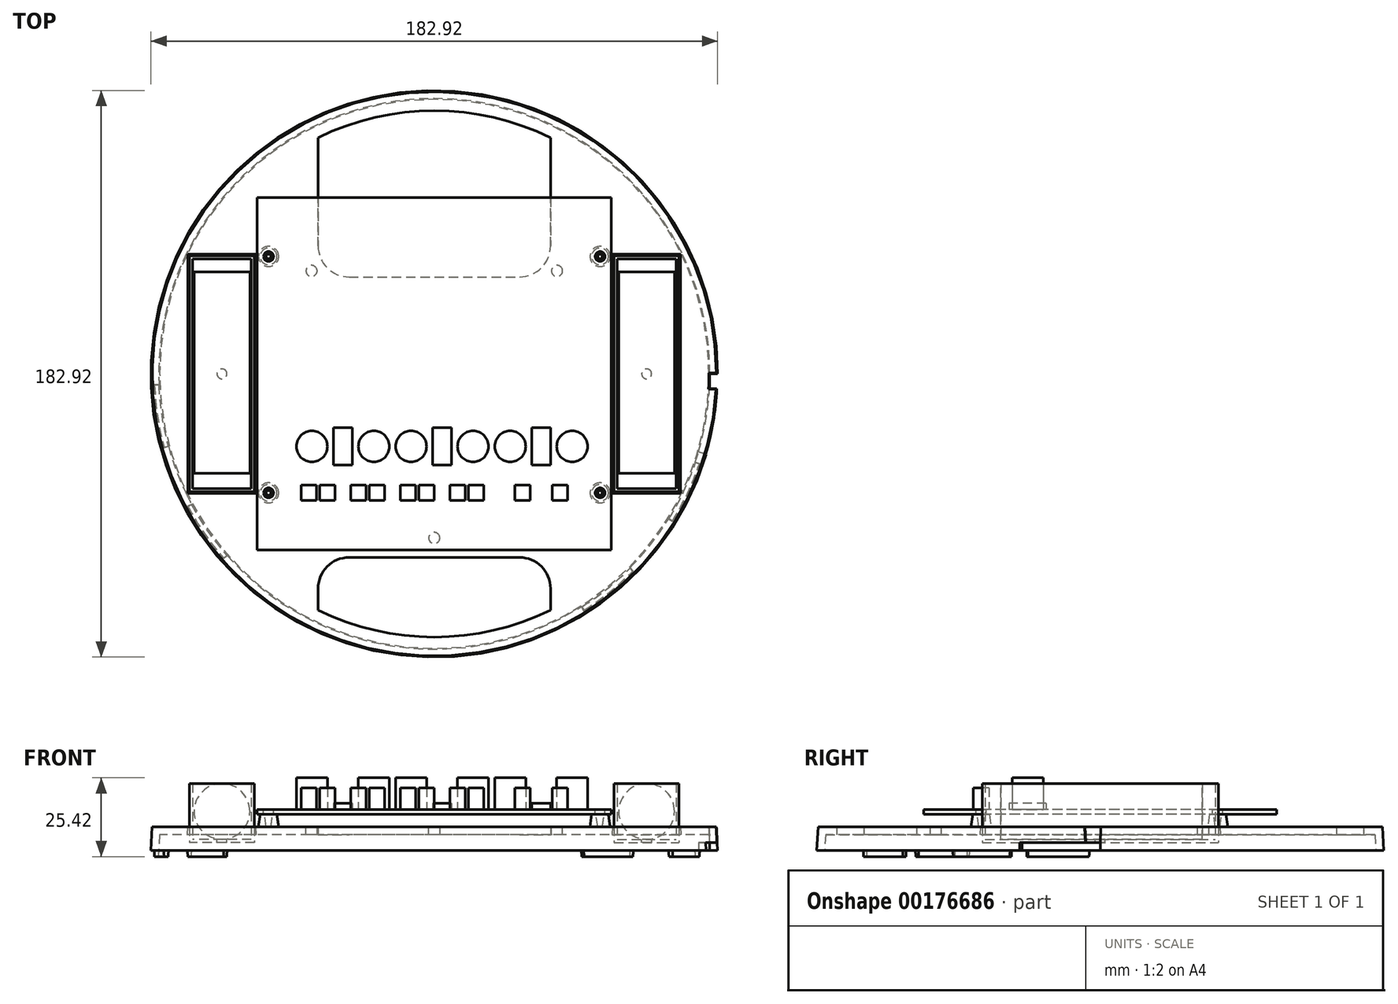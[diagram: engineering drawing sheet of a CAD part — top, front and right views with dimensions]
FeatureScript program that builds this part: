
annotation { "Feature Type Name" : "Feature", "Feature Type Description" : "" }
export const myFeature = defineFeature(function(context is Context, id is Id, definition is map)
    precondition{}
    {
        {
            assignVariable(context, id + "F0", {"name" : "h_env", "anyValue" : 230});
        }
        {
            var Q0;
            Q0=qCreatedBy(makeId("Top.planeOp"),FACE);
            var sketch = newSketch(context, id + "F1", { "sketchPlane" : qUnion([Q0])});
            skCircle(sketch, "E0", {"center": v(0, 0) * mm, "radius": 94 * mm});
            skSolve(sketch);
        }
        {
            var Q0;
            Q0=qCreatedBy(makeId("Top.planeOp"),FACE);
            cPlane(context, id + "F2", {"entities" : qUnion([Q0]), "cplaneType" : CPlaneType.OFFSET, "offset" : (getVariable(context, 'h_env')) * mm, "width" : 152.4 * mm, "height" : 152.4 * mm});
        }
        {
            var Q0;
            Q0=makeQuery(id+"F1.imprint","IMPRINT",FACE,{"disambiguationData":[TD([[makeQuery(id+"F1.imprint","IMPRINT",EDGE,{"derivedFrom":sQuery(id+"F1.wireOp",EDGE,"E0")}),1.0]])]});
            var Q1;
            Q1=sQuery(id+"F1.wireOp",EDGE,"E0");
            var Q2;
            Q2=qCreatedBy(id+"F2.planeOp",FACE);
            extrude(context, id + "F3", {"entities" : qUnion([Q0]), "bodyType" : ToolBodyType.SURFACE, "surfaceEntities" : qUnion([Q1]), "endBound" : BoundingType.UP_TO_SURFACE, "endBoundEntityFace" : qUnion([Q2]), "depth" : 25.4 * mm});
        }
        {
            var Q0;
            Q0=qCreatedBy(makeId("Right.planeOp"),FACE);
            var sketch = newSketch(context, id + "F4", { "sketchPlane" : qUnion([Q0])});
            skLineSegment(sketch, "E1", {"start": v(0, 0) * mm, "end": v(0, 230) * mm, "construction": true});
            skSolve(sketch);
        }
        {
            assignVariable(context, id + "F5", {"name" : "t", "anyValue" : 2.54});
        }
        {
            assignVariable(context, id + "F6", {"name" : "h_primary", "anyValue" : 19.05});
        }
        {
            assignVariable(context, id + "F7", {"name" : "draft", "anyValue" : 3});
        }
        {
            var Q0;
            Q0=qCreatedBy(id+"F2.planeOp",FACE);
            cPlane(context, id + "F8", {"entities" : qUnion([Q0]), "cplaneType" : CPlaneType.OFFSET, "offset" : (getVariable(context, 'h_primary')) * mm, "oppositeDirection" : true, "width" : 152.4 * mm, "height" : 152.4 * mm});
        }
        {
            var Q0;
            Q0=qCreatedBy(id+"F8.planeOp",FACE);
            var sketch = newSketch(context, id + "F9", { "sketchPlane" : qUnion([Q0])});
            skCircle(sketch, "E2", {"center": v(0, 0) * mm, "radius": 91.46 * mm});
            skSolve(sketch);
        }
        {
            var Q0;
            Q0=makeQuery(id+"F9.imprint","IMPRINT",FACE,{"disambiguationData":[TD([[makeQuery(id+"F9.imprint","IMPRINT",EDGE,{"derivedFrom":sQuery(id+"F9.wireOp",EDGE,"E2")}),1.0]])]});
            extrude(context, id + "F10", {"entities" : qUnion([Q0]), "depth" : (3 * getVariable(context, 't')) * mm, "hasDraft" : true, "draftAngle" : (getVariable(context, 'draft')) * degree, "draftPullDirection" : true});
        }
        {
            var Q0;
            Q0=makeQuery(id+"F10.opExtrude","CAP_FACE",FACE,{"disambiguationData":[OSD([sQuery(id+"F9.wireOp",EDGE,"E2")])],"isStart":true});
            shell(context, id + "F11", {"entities" : qUnion([Q0]), "thickness" : (getVariable(context, 't')) * mm});
        }
        {
            var Q0;
            Q0=makeQuery(id+"F10.opExtrude","CAP_FACE",FACE,{"disambiguationData":[OSD([sQuery(id+"F9.wireOp",EDGE,"E2")])],"isStart":true});
            var sketch = newSketch(context, id + "F12", { "sketchPlane" : qUnion([Q0])});
            skLineSegment(sketch, "E3", {"start": v(0, 0) * mm, "end": v(88.34, 23.67) * mm, "construction": true});
            skLineSegment(sketch, "E4", {"start": v(0, 0) * mm, "end": v(91.46, 0) * mm, "construction": true});
            skLineSegment(sketch, "E5", {"start": v(0, 0) * mm, "end": v(87.7, 25.98) * mm, "construction": true});
            skCircle(sketch, "E6.0", {"center": v(0, 0) * mm, "radius": 88.65 * mm});
            skArc(sketch, "E7", {"start": v(88.65, 0) * mm, "mid": v(87.73, 12.72) * mm, "end": v(85, 25.18) * mm});
            skLineSegment(sketch, "E8", {"start": v(87.7, 25.98) * mm, "end": v(85, 25.18) * mm});
            skLineSegment(sketch, "E9", {"start": v(91.46, 0) * mm, "end": v(88.65, 0) * mm});
            skSolve(sketch);
        }
        {
            var Q0;
            {var subQ0=sQuery(id+"F12.wireOp",EDGE,"E8");var subQ1=sQuery(id+"F9.wireOp",EDGE,"E2");var subQ2=makeQuery(id+"F10.opExtrude","CAP_EDGE",EDGE,{"disambiguationData":[OSD([subQ1])],"isStart":true});var subQ3=makeQuery(id+"F12.imprint","INTERSECT",VERTEX,{"derivedFrom":[subQ2,subQ0]});Q0=makeQuery(id+"F12.imprint","IMPRINT",FACE,{"disambiguationData":[TD([[makeQuery(id+"F12.imprint","IMPRINT",EDGE,{"disambiguationData":[TD([[subQ3,-1.0]])],"derivedFrom":subQ2}),-1.0]])]});}
            var Q1;
            {var subQ0=sQuery(id+"F12.wireOp",EDGE,"E8");var subQ1=sQuery(id+"F12.wireOp",EDGE,"E6.0");var subQ2=makeQuery(id+"F12.imprint","INTERSECT",VERTEX,{"derivedFrom":[subQ1,subQ0]});Q1=makeQuery(id+"F12.imprint","IMPRINT",FACE,{"disambiguationData":[TD([[makeQuery(id+"F12.imprint","IMPRINT",EDGE,{"disambiguationData":[TD([[subQ2,-1.0]])],"derivedFrom":subQ1}),1.0]])]});}
            extrude(context, id + "F13", {"entities" : qUnion([Q0, Q1]), "operationType" : NewBodyOperationType.REMOVE, "oppositeDirection" : true, "depth" : (getVariable(context, 't')) * mm});
        }
        {
            var Q0;
            Q0=makeQuery(id+"F13.boolean.opBoolean","COPY",FACE,{"derivedFrom":makeQuery(id+"F13.opExtrude","CAP_FACE",FACE,{"disambiguationData":[OSD([sQuery(id+"F9.wireOp",EDGE,"E2"),sQuery(id+"F12.wireOp",EDGE,"E6.0"),sQuery(id+"F12.wireOp",EDGE,"E8"),sQuery(id+"F12.wireOp",EDGE,"E9")])],"isStart":false})});
            var sketch = newSketch(context, id + "F14", { "sketchPlane" : qUnion([Q0])});
            skArc(sketch, "E10.0", {"start": v(91.33, 0) * mm, "mid": v(90.38, 13.1) * mm, "end": v(87.57, 25.94) * mm});
            skCircle(sketch, "E11.0", {"center": v(0, 0) * mm, "radius": 88.65 * mm});
            skLineSegment(sketch, "E12.0", {"start": v(91.33, 0) * mm, "end": v(88.65, 0) * mm});
            skPoint(sketch, "E13.orphan", {"position": v(88.78, 0) * mm});
            skLineSegment(sketch, "E14", {"start": v(0, 0) * mm, "end": v(91.33, 0) * mm, "construction": true});
            skLineSegment(sketch, "E15", {"start": v(0, 0) * mm, "end": v(91.2, 4.78) * mm, "construction": true});
            skLineSegment(sketch, "E16", {"start": v(91.2, 4.78) * mm, "end": v(88.53, 4.64) * mm});
            skSolve(sketch);
        }
        {
            var Q0;
            {var subQ0=sQuery(id+"F14.wireOp",EDGE,"E12.0");var subQ1=sQuery(id+"F14.wireOp",EDGE,"E10.0");var subQ2=makeQuery(id+"F14.imprint","INTERSECT",VERTEX,{"derivedFrom":[subQ1,subQ0]});Q0=makeQuery(id+"F14.imprint","IMPRINT",FACE,{"disambiguationData":[TD([[makeQuery(id+"F14.imprint","IMPRINT",EDGE,{"disambiguationData":[TD([[subQ2,-1.0]])],"derivedFrom":subQ1}),1.0]])]});}
            var Q1;
            Q1=makeQuery(id+"F10.opExtrude","CAP_FACE",FACE,{"disambiguationData":[OSD([sQuery(id+"F9.wireOp",EDGE,"E2")])],"isStart":false});
            extrude(context, id + "F15", {"entities" : qUnion([Q0]), "operationType" : NewBodyOperationType.REMOVE, "endBound" : BoundingType.UP_TO_SURFACE, "oppositeDirection" : true, "endBoundEntityFace" : qUnion([Q1]), "depth" : 25 * mm, "hasDraft" : true, "draftAngle" : 3 * degree});
        }
        {
            var Q0;
            Q0=makeQuery(id+"F9.imprint","IMPRINT",FACE,{"disambiguationData":[TD([[makeQuery(id+"F9.imprint","IMPRINT",EDGE,{"derivedFrom":sQuery(id+"F9.wireOp",EDGE,"E2")}),1.0]])]});
            var sketch = newSketch(context, id + "F16", { "sketchPlane" : qUnion([Q0])});
            skArc(sketch, "E17", {"start": v(-37.5, 76.28) * mm, "mid": v(0, 85) * mm, "end": v(37.5, 76.28) * mm});
            skLineSegment(sketch, "E18.bottom", {"start": v(-37.5, 76.28) * mm, "end": v(37.5, 76.28) * mm, "construction": true});
            skLineSegment(sketch, "E18.top", {"start": v(-27.5, 31.28) * mm, "end": v(27.5, 31.28) * mm});
            skLineSegment(sketch, "E18.left", {"start": v(-37.5, 76.28) * mm, "end": v(-37.5, 41.28) * mm});
            skLineSegment(sketch, "E18.right", {"start": v(37.5, 76.28) * mm, "end": v(37.5, 41.28) * mm});
            skPoint(sketch, "E19.visualSharp", {"position": v(37.5, 31.28) * mm});
            skArc(sketch, "E19.filletArc", {"start": v(27.5, 31.28) * mm, "mid": v(34.57, 34.2) * mm, "end": v(37.5, 41.28) * mm});
            skPoint(sketch, "E20.visualSharp", {"position": v(-37.5, 31.28) * mm});
            skArc(sketch, "E20.filletArc", {"start": v(-37.5, 41.28) * mm, "mid": v(-34.57, 34.2) * mm, "end": v(-27.5, 31.28) * mm});
            skArc(sketch, "E21", {"start": v(37.5, -76.28) * mm, "mid": v(0, -85) * mm, "end": v(-37.5, -76.28) * mm});
            skLineSegment(sketch, "E22.bottom", {"start": v(-37.5, -76.28) * mm, "end": v(37.5, -76.28) * mm, "construction": true});
            skLineSegment(sketch, "E22.top", {"start": v(-27.5, -59.28) * mm, "end": v(27.5, -59.28) * mm});
            skLineSegment(sketch, "E22.left", {"start": v(-37.5, -76.28) * mm, "end": v(-37.5, -69.28) * mm});
            skLineSegment(sketch, "E22.right", {"start": v(37.5, -76.28) * mm, "end": v(37.5, -69.28) * mm});
            skPoint(sketch, "E23.visualSharp", {"position": v(-37.5, -59.28) * mm});
            skArc(sketch, "E23.filletArc", {"start": v(-27.5, -59.28) * mm, "mid": v(-34.57, -62.2) * mm, "end": v(-37.5, -69.28) * mm});
            skPoint(sketch, "E24.visualSharp", {"position": v(37.5, -59.28) * mm});
            skArc(sketch, "E24.filletArc", {"start": v(37.5, -69.28) * mm, "mid": v(34.57, -62.2) * mm, "end": v(27.5, -59.28) * mm});
            skSolve(sketch);
        }
        {
            var Q0;
            Q0 = qSketchRegion(id + "F16", true);
            var Q1;
            Q1=sQuery(id+"F16.wireOp",EDGE,"E18.bottom");
            var Q2;
            Q2=makeQuery(id+"F10.opExtrude","CAP_FACE",FACE,{"disambiguationData":[OSD([sQuery(id+"F9.wireOp",EDGE,"E2")])],"isStart":false});
            extrude(context, id + "F17", {"entities" : qUnion([Q0]), "operationType" : NewBodyOperationType.REMOVE, "surfaceEntities" : qUnion([Q1]), "endBound" : BoundingType.UP_TO_SURFACE, "endBoundEntityFace" : qUnion([Q2]), "depth" : 25 * mm});
        }
        {
            var Q0;
            Q0=qCreatedBy(id+"F8.planeOp",FACE);
            cPlane(context, id + "F18", {"entities" : qUnion([Q0]), "cplaneType" : CPlaneType.OFFSET, "offset" : (5 * getVariable(context, 't') - 1.08) * mm, "width" : 152.4 * mm, "height" : 152.4 * mm});
        }
        {
            assignVariable(context, id + "F19", {"name" : "h_pcb", "anyValue" : 1.6});
        }
        {
            var Q0;
            Q0=qCreatedBy(id+"F18.planeOp",FACE);
            var sketch = newSketch(context, id + "F20", { "sketchPlane" : qUnion([Q0])});
            skLineSegment(sketch, "E25.bottom", {"start": v(-57.15, 56.91) * mm, "end": v(57.15, 56.9) * mm});
            skLineSegment(sketch, "E25.top", {"start": v(-57.15, -56.9) * mm, "end": v(57.15, -56.91) * mm});
            skLineSegment(sketch, "E25.left", {"start": v(-57.15, 56.91) * mm, "end": v(-57.15, -56.91) * mm});
            skLineSegment(sketch, "E25.right", {"start": v(57.15, 56.91) * mm, "end": v(57.15, -56.91) * mm});
            skPoint(sketch, "E26", {"position": v(57.15, 0) * mm});
            skPoint(sketch, "E27", {"position": v(0, 56.9) * mm});
            skSolve(sketch);
        }
        {
            var Q0;
            Q0=makeQuery(id+"F20.imprint","IMPRINT",FACE,{"disambiguationData":[TD([[makeQuery(id+"F20.imprint","IMPRINT",EDGE,{"derivedFrom":sQuery(id+"F20.wireOp",EDGE,"E25.bottom")}),-1.0]])]});
            extrude(context, id + "F21", {"entities" : qUnion([Q0]), "depth" : (getVariable(context, 'h_pcb')) * mm});
        }
        {
            var Q0;
            Q0=makeQuery(id+"F21.opExtrude","CAP_FACE",FACE,{"disambiguationData":[OSD([sQuery(id+"F20.wireOp",EDGE,"E25.bottom"),sQuery(id+"F20.wireOp",EDGE,"E25.top"),sQuery(id+"F20.wireOp",EDGE,"E25.left"),sQuery(id+"F20.wireOp",EDGE,"E25.right")])],"isStart":false});
            var sketch = newSketch(context, id + "F22", { "sketchPlane" : qUnion([Q0])});
            skCircle(sketch, "E28", {"center": v(53.5, 37.9) * mm, "radius": 1.6 * mm});
            skCircle(sketch, "E29.0.1.0", {"center": v(53.5, -38.43) * mm, "radius": 1.6 * mm});
            skCircle(sketch, "E29.1.0.0", {"center": v(-53.5, 37.9) * mm, "radius": 1.6 * mm});
            skCircle(sketch, "E29.1.1.0", {"center": v(-53.5, -38.43) * mm, "radius": 1.6 * mm});
            skLineSegment(sketch, "E29.direction1", {"start": v(53.5, 37.9) * mm, "end": v(-53.5, 37.9) * mm, "construction": true});
            skLineSegment(sketch, "E29.direction2", {"start": v(53.5, 37.9) * mm, "end": v(53.5, -38.43) * mm, "construction": true});
            skSolve(sketch);
        }
        {
            var Q0;
            Q0 = qSketchRegion(id + "F22", true);
            extrude(context, id + "F23", {"entities" : qUnion([Q0]), "operationType" : NewBodyOperationType.REMOVE, "endBound" : BoundingType.UP_TO_NEXT, "oppositeDirection" : true, "depth" : 25.4 * mm});
        }
        {
            var Q0;
            Q0=makeQuery(id+"F10.opExtrude","CAP_FACE",FACE,{"disambiguationData":[OSD([sQuery(id+"F9.wireOp",EDGE,"E2")])],"isStart":false});
            var sketch = newSketch(context, id + "F24", { "sketchPlane" : qUnion([Q0])});
            skCircle(sketch, "E30.0", {"center": v(53.5, 37.9) * mm, "radius": 1.6 * mm, "construction": true});
            skCircle(sketch, "E31.0", {"center": v(53.5, -38.43) * mm, "radius": 1.6 * mm, "construction": true});
            skCircle(sketch, "E32.0", {"center": v(-53.5, -38.43) * mm, "radius": 1.6 * mm, "construction": true});
            skCircle(sketch, "E33.0", {"center": v(-53.5, 37.9) * mm, "radius": 1.6 * mm, "construction": true});
            skCircle(sketch, "E34", {"center": v(53.5, 37.9) * mm, "radius": 3.25 * mm});
            skCircle(sketch, "E35", {"center": v(53.5, -38.43) * mm, "radius": 3.25 * mm});
            skCircle(sketch, "E36", {"center": v(-53.5, -38.43) * mm, "radius": 3.25 * mm});
            skCircle(sketch, "E37", {"center": v(-53.5, 37.9) * mm, "radius": 3.25 * mm});
            skCircle(sketch, "E38", {"center": v(53.5, 37.9) * mm, "radius": 0.75 * mm});
            skCircle(sketch, "E39", {"center": v(-53.5, 37.9) * mm, "radius": 0.75 * mm});
            skCircle(sketch, "E40", {"center": v(-53.5, -38.43) * mm, "radius": 0.75 * mm});
            skCircle(sketch, "E41", {"center": v(53.5, -38.43) * mm, "radius": 0.75 * mm});
            skSolve(sketch);
        }
        {
            var Q0;
            Q0 = qSketchRegion(id + "F24", true);
            var Q1;
            Q1=sQuery(id+"F24.wireOp",EDGE,"D2eIxqeC-2rqa-4NXI-Nvdh-6eyWbRgn4P1Z");
            var Q2;
            Q2=makeQuery(id+"F21.opExtrude","CAP_FACE",FACE,{"disambiguationData":[OSD([sQuery(id+"F20.wireOp",EDGE,"E25.bottom"),sQuery(id+"F20.wireOp",EDGE,"E25.top"),sQuery(id+"F20.wireOp",EDGE,"E25.left"),sQuery(id+"F20.wireOp",EDGE,"E25.right")])],"isStart":true});
            extrude(context, id + "F25", {"entities" : qUnion([Q0]), "operationType" : NewBodyOperationType.ADD, "surfaceEntities" : qUnion([Q1]), "endBound" : BoundingType.UP_TO_SURFACE, "endBoundEntityFace" : qUnion([Q2]), "depth" : 25.4 * mm, "hasDraft" : true, "draftAngle" : 8 * degree, "draftPullDirection" : true});
        }
        {
            var Q0;
            {var subQ4=sQuery(id+"F9.wireOp",EDGE,"E2");Q0=makeQuery(id+"F25.boolean.opBoolean","SPLIT",FACE,{"disambiguationData":[TD([makeQuery(id+"F10.opExtrude","SWEPT_FACE",FACE,{"disambiguationData":[OSD([subQ4])]})])],"derivedFrom":makeQuery(id+"F10.opExtrude","CAP_FACE",FACE,{"disambiguationData":[OSD([subQ4])],"isStart":false})});}
            var sketch = newSketch(context, id + "F26", { "sketchPlane" : qUnion([Q0])});
            skCircle(sketch, "E42.0", {"center": v(0, 0) * mm, "radius": 94 * mm, "construction": true});
            skLineSegment(sketch, "E43", {"start": v(0, 0) * mm, "end": v(0, -94) * mm, "construction": true});
            skLineSegment(sketch, "E44", {"start": v(0, 0) * mm, "end": v(-72, 60.42) * mm, "construction": true});
            skCircle(sketch, "E45", {"center": v(0, -53) * mm, "radius": 1.8 * mm});
            skCircle(sketch, "E46", {"center": v(-39.61, 33.24) * mm, "radius": 1.8 * mm});
            skCircle(sketch, "E47.MirrorC", {"center": v(39.61, 33.24) * mm, "radius": 1.8 * mm});
            skSolve(sketch);
        }
        {
            var Q0;
            Q0 = qSketchRegion(id + "F26", true);
            var Q1;
            {var subQ0=sQuery(id+"F9.wireOp",EDGE,"E2");Q1=makeQuery(id+"F11.opShell","OFFSET_FACE",FACE,{"disambiguationData":[OSD([subQ0]),TDD([makeQuery(id+"F10.opExtrude","CAP_FACE",FACE,{"disambiguationData":[OSD([subQ0])],"isStart":false})])]});}
            extrude(context, id + "F27", {"entities" : qUnion([Q0]), "operationType" : NewBodyOperationType.REMOVE, "endBound" : BoundingType.UP_TO_SURFACE, "oppositeDirection" : true, "endBoundEntityFace" : qUnion([Q1]), "depth" : 25 * mm});
        }
        {
            var Q0;
            Q0=makeQuery(id+"F21.opExtrude","CAP_FACE",FACE,{"disambiguationData":[OSD([sQuery(id+"F20.wireOp",EDGE,"E25.bottom"),sQuery(id+"F20.wireOp",EDGE,"E25.top"),sQuery(id+"F20.wireOp",EDGE,"E25.left"),sQuery(id+"F20.wireOp",EDGE,"E25.right")])],"isStart":false});
            var sketch = newSketch(context, id + "F28", { "sketchPlane" : qUnion([Q0])});
            skCircle(sketch, "E48.0", {"center": v(-53.5, -38.43) * mm, "radius": 1.6 * mm, "construction": true});
            skCircle(sketch, "E49.0", {"center": v(53.5, -38.43) * mm, "radius": 1.6 * mm, "construction": true});
            skLineSegment(sketch, "E50", {"start": v(-53.5, -38.43) * mm, "end": v(53.5, -38.43) * mm, "construction": true});
            skLineSegment(sketch, "E51.bottom", {"start": v(-38, -35.93) * mm, "end": v(-43, -35.93) * mm});
            skLineSegment(sketch, "E51.top", {"start": v(-38, -40.93) * mm, "end": v(-43, -40.93) * mm});
            skLineSegment(sketch, "E51.left", {"start": v(-38, -35.93) * mm, "end": v(-38, -40.93) * mm});
            skLineSegment(sketch, "E51.right", {"start": v(-43, -35.93) * mm, "end": v(-43, -40.93) * mm});
            skPoint(sketch, "E51.middle", {"position": v(-40.5, -38.43) * mm});
            skLineSegment(sketch, "E52.bottom", {"start": v(-37, -35.93) * mm, "end": v(-32, -35.93) * mm});
            skLineSegment(sketch, "E52.top", {"start": v(-37, -40.93) * mm, "end": v(-32, -40.93) * mm});
            skLineSegment(sketch, "E52.left", {"start": v(-37, -35.93) * mm, "end": v(-37, -40.93) * mm});
            skLineSegment(sketch, "E52.right", {"start": v(-32, -35.93) * mm, "end": v(-32, -40.93) * mm});
            skPoint(sketch, "E52.middle", {"position": v(-34.5, -38.43) * mm});
            skLineSegment(sketch, "E53.bottom", {"start": v(-27, -35.93) * mm, "end": v(-22, -35.93) * mm});
            skLineSegment(sketch, "E53.top", {"start": v(-27, -40.93) * mm, "end": v(-22, -40.93) * mm});
            skLineSegment(sketch, "E53.left", {"start": v(-27, -35.93) * mm, "end": v(-27, -40.93) * mm});
            skLineSegment(sketch, "E53.right", {"start": v(-22, -35.93) * mm, "end": v(-22, -40.93) * mm});
            skPoint(sketch, "E53.middle", {"position": v(-24.5, -38.43) * mm});
            skLineSegment(sketch, "E54.bottom", {"start": v(-21, -35.93) * mm, "end": v(-16, -35.93) * mm});
            skLineSegment(sketch, "E54.top", {"start": v(-21, -40.93) * mm, "end": v(-16, -40.93) * mm});
            skLineSegment(sketch, "E54.left", {"start": v(-21, -35.93) * mm, "end": v(-21, -40.93) * mm});
            skLineSegment(sketch, "E54.right", {"start": v(-16, -35.93) * mm, "end": v(-16, -40.93) * mm});
            skPoint(sketch, "E54.middle", {"position": v(-18.5, -38.43) * mm});
            skLineSegment(sketch, "E55.bottom", {"start": v(-11, -35.93) * mm, "end": v(-6, -35.93) * mm});
            skLineSegment(sketch, "E55.top", {"start": v(-11, -40.93) * mm, "end": v(-6, -40.93) * mm});
            skLineSegment(sketch, "E55.left", {"start": v(-11, -35.93) * mm, "end": v(-11, -40.93) * mm});
            skLineSegment(sketch, "E55.right", {"start": v(-6, -35.93) * mm, "end": v(-6, -40.93) * mm});
            skPoint(sketch, "E55.middle", {"position": v(-8.5, -38.43) * mm});
            skLineSegment(sketch, "E56.bottom", {"start": v(-5, -35.93) * mm, "end": v(0, -35.93) * mm});
            skLineSegment(sketch, "E56.top", {"start": v(-5, -40.93) * mm, "end": v(0, -40.93) * mm});
            skLineSegment(sketch, "E56.left", {"start": v(-5, -35.93) * mm, "end": v(-5, -40.93) * mm});
            skLineSegment(sketch, "E56.right", {"start": v(0, -35.93) * mm, "end": v(0, -40.93) * mm});
            skPoint(sketch, "E56.middle", {"position": v(-2.5, -38.43) * mm});
            skLineSegment(sketch, "E57.bottom", {"start": v(5, -35.93) * mm, "end": v(10, -35.93) * mm});
            skLineSegment(sketch, "E57.top", {"start": v(5, -40.93) * mm, "end": v(10, -40.93) * mm});
            skLineSegment(sketch, "E57.left", {"start": v(5, -35.93) * mm, "end": v(5, -40.93) * mm});
            skLineSegment(sketch, "E57.right", {"start": v(10, -35.93) * mm, "end": v(10, -40.93) * mm});
            skPoint(sketch, "E57.middle", {"position": v(7.5, -38.43) * mm});
            skLineSegment(sketch, "E58.bottom", {"start": v(11, -35.93) * mm, "end": v(16, -35.93) * mm});
            skLineSegment(sketch, "E58.top", {"start": v(11, -40.93) * mm, "end": v(16, -40.93) * mm});
            skLineSegment(sketch, "E58.left", {"start": v(11, -35.93) * mm, "end": v(11, -40.93) * mm});
            skLineSegment(sketch, "E58.right", {"start": v(16, -35.93) * mm, "end": v(16, -40.93) * mm});
            skPoint(sketch, "E58.middle", {"position": v(13.5, -38.43) * mm});
            skLineSegment(sketch, "E59.bottom", {"start": v(26, -35.93) * mm, "end": v(31, -35.93) * mm});
            skLineSegment(sketch, "E59.top", {"start": v(26, -40.93) * mm, "end": v(31, -40.93) * mm});
            skLineSegment(sketch, "E59.left", {"start": v(26, -35.93) * mm, "end": v(26, -40.93) * mm});
            skLineSegment(sketch, "E59.right", {"start": v(31, -35.93) * mm, "end": v(31, -40.93) * mm});
            skPoint(sketch, "E59.middle", {"position": v(28.5, -38.43) * mm});
            skLineSegment(sketch, "E60.bottom", {"start": v(38, -35.93) * mm, "end": v(43, -35.93) * mm});
            skLineSegment(sketch, "E60.top", {"start": v(38, -40.93) * mm, "end": v(43, -40.93) * mm});
            skLineSegment(sketch, "E60.left", {"start": v(38, -35.93) * mm, "end": v(38, -40.93) * mm});
            skLineSegment(sketch, "E60.right", {"start": v(43, -35.93) * mm, "end": v(43, -40.93) * mm});
            skPoint(sketch, "E60.middle", {"position": v(40.5, -38.43) * mm});
            skSolve(sketch);
        }
        {
            var Q0;
            Q0 = qSketchRegion(id + "F28", true);
            extrude(context, id + "F29", {"entities" : qUnion([Q0]), "operationType" : NewBodyOperationType.ADD, "depth" : 7 * mm});
        }
        {
            var Q0;
            Q0=makeQuery(id+"F21.opExtrude","CAP_FACE",FACE,{"disambiguationData":[OSD([sQuery(id+"F20.wireOp",EDGE,"E25.bottom"),sQuery(id+"F20.wireOp",EDGE,"E25.top"),sQuery(id+"F20.wireOp",EDGE,"E25.left"),sQuery(id+"F20.wireOp",EDGE,"E25.right")])],"isStart":false});
            var sketch = newSketch(context, id + "F30", { "sketchPlane" : qUnion([Q0])});
            skLineSegment(sketch, "E61.bottom", {"start": v(-26.5, -17.43) * mm, "end": v(-32.5, -17.43) * mm});
            skLineSegment(sketch, "E61.top", {"start": v(-26.5, -29.43) * mm, "end": v(-32.5, -29.43) * mm});
            skLineSegment(sketch, "E61.left", {"start": v(-26.5, -17.43) * mm, "end": v(-26.5, -29.43) * mm});
            skLineSegment(sketch, "E61.right", {"start": v(-32.5, -17.43) * mm, "end": v(-32.5, -29.43) * mm});
            skPoint(sketch, "E61.middle", {"position": v(-29.5, -23.43) * mm});
            skLineSegment(sketch, "E62.bottom", {"start": v(-0.5, -17.43) * mm, "end": v(5.5, -17.43) * mm});
            skLineSegment(sketch, "E62.top", {"start": v(-0.5, -29.43) * mm, "end": v(5.5, -29.43) * mm});
            skLineSegment(sketch, "E62.left", {"start": v(-0.5, -17.43) * mm, "end": v(-0.5, -29.43) * mm});
            skLineSegment(sketch, "E62.right", {"start": v(5.5, -17.43) * mm, "end": v(5.5, -29.43) * mm});
            skPoint(sketch, "E62.middle", {"position": v(2.5, -23.43) * mm});
            skLineSegment(sketch, "E63.bottom", {"start": v(31.5, -17.43) * mm, "end": v(37.5, -17.43) * mm});
            skLineSegment(sketch, "E63.top", {"start": v(31.5, -29.43) * mm, "end": v(37.5, -29.43) * mm});
            skLineSegment(sketch, "E63.left", {"start": v(31.5, -17.43) * mm, "end": v(31.5, -29.43) * mm});
            skLineSegment(sketch, "E63.right", {"start": v(37.5, -17.43) * mm, "end": v(37.5, -29.43) * mm});
            skPoint(sketch, "E63.middle", {"position": v(34.5, -23.43) * mm});
            skCircle(sketch, "E64.0", {"center": v(-53.5, -38.43) * mm, "radius": 1.6 * mm, "construction": true});
            skCircle(sketch, "E65.0", {"center": v(53.5, -38.43) * mm, "radius": 1.6 * mm, "construction": true});
            skLineSegment(sketch, "E66", {"start": v(53.5, -38.43) * mm, "end": v(-53.5, -38.43) * mm, "construction": true});
            skSolve(sketch);
        }
        {
            var Q0;
            Q0 = qSketchRegion(id + "F30", true);
            extrude(context, id + "F31", {"entities" : qUnion([Q0]), "operationType" : NewBodyOperationType.ADD, "depth" : 2 * mm});
        }
        {
            var Q0;
            Q0=makeQuery(id+"F21.opExtrude","CAP_FACE",FACE,{"disambiguationData":[OSD([sQuery(id+"F20.wireOp",EDGE,"E25.bottom"),sQuery(id+"F20.wireOp",EDGE,"E25.top"),sQuery(id+"F20.wireOp",EDGE,"E25.left"),sQuery(id+"F20.wireOp",EDGE,"E25.right")])],"isStart":false});
            var sketch = newSketch(context, id + "F32", { "sketchPlane" : qUnion([Q0])});
            skLineSegment(sketch, "E67.0.0", {"start": v(-26.5, -29.43) * mm, "end": v(-26.5, -17.43) * mm, "construction": true});
            skLineSegment(sketch, "E67.0.1", {"start": v(-26.5, -17.43) * mm, "end": v(-32.5, -17.43) * mm, "construction": true});
            skLineSegment(sketch, "E67.0.2", {"start": v(-32.5, -17.43) * mm, "end": v(-32.5, -29.43) * mm, "construction": true});
            skLineSegment(sketch, "E67.0.3", {"start": v(-32.5, -29.43) * mm, "end": v(-26.5, -29.43) * mm, "construction": true});
            skLineSegment(sketch, "E68.0.0", {"start": v(5.5, -17.43) * mm, "end": v(-0.5, -17.43) * mm, "construction": true});
            skLineSegment(sketch, "E68.0.1", {"start": v(-0.5, -17.43) * mm, "end": v(-0.5, -29.43) * mm, "construction": true});
            skLineSegment(sketch, "E68.0.2", {"start": v(-0.5, -29.43) * mm, "end": v(5.5, -29.43) * mm, "construction": true});
            skLineSegment(sketch, "E68.0.3", {"start": v(5.5, -29.43) * mm, "end": v(5.5, -17.43) * mm, "construction": true});
            skLineSegment(sketch, "E69.0.0", {"start": v(37.5, -17.43) * mm, "end": v(31.5, -17.43) * mm, "construction": true});
            skLineSegment(sketch, "E69.0.1", {"start": v(31.5, -17.43) * mm, "end": v(31.5, -29.43) * mm, "construction": true});
            skLineSegment(sketch, "E69.0.2", {"start": v(31.5, -29.43) * mm, "end": v(37.5, -29.43) * mm, "construction": true});
            skLineSegment(sketch, "E69.0.3", {"start": v(37.5, -29.43) * mm, "end": v(37.5, -17.43) * mm, "construction": true});
            skLineSegment(sketch, "E70", {"start": v(-29.5, -17.43) * mm, "end": v(-29.5, -29.43) * mm, "construction": true});
            skLineSegment(sketch, "E71", {"start": v(-26.5, -23.43) * mm, "end": v(-32.5, -23.43) * mm, "construction": true});
            skCircle(sketch, "E72", {"center": v(-39.5, -23.43) * mm, "radius": 5 * mm});
            skCircle(sketch, "E73", {"center": v(-19.5, -23.43) * mm, "radius": 5 * mm});
            skPoint(sketch, "E73.centerSnap0", {"position": v(-29.5, -23.43) * mm});
            skLineSegment(sketch, "E74", {"start": v(2.5, -17.43) * mm, "end": v(2.5, -29.43) * mm, "construction": true});
            skLineSegment(sketch, "E75", {"start": v(-0.5, -23.43) * mm, "end": v(5.5, -23.43) * mm, "construction": true});
            skLineSegment(sketch, "E76", {"start": v(31.5, -23.43) * mm, "end": v(37.5, -23.43) * mm, "construction": true});
            skLineSegment(sketch, "E77", {"start": v(34.5, -17.43) * mm, "end": v(34.5, -29.43) * mm, "construction": true});
            skCircle(sketch, "E78", {"center": v(-7.5, -23.43) * mm, "radius": 5 * mm});
            skCircle(sketch, "E79", {"center": v(12.5, -23.43) * mm, "radius": 5 * mm});
            skPoint(sketch, "E79.centerSnap0", {"position": v(2.5, -23.43) * mm});
            skCircle(sketch, "E80", {"center": v(24.5, -23.43) * mm, "radius": 5 * mm});
            skCircle(sketch, "E81", {"center": v(44.5, -23.43) * mm, "radius": 5 * mm});
            skPoint(sketch, "E81.centerSnap0", {"position": v(34.5, -23.43) * mm});
            skLineSegment(sketch, "E82", {"start": v(-29.5, -23.43) * mm, "end": v(-39.5, -23.43) * mm, "construction": true});
            skLineSegment(sketch, "E83", {"start": v(-29.5, -23.43) * mm, "end": v(-19.5, -23.43) * mm, "construction": true});
            skLineSegment(sketch, "E84", {"start": v(-7.5, -23.43) * mm, "end": v(2.5, -23.43) * mm, "construction": true});
            skLineSegment(sketch, "E85", {"start": v(2.5, -23.43) * mm, "end": v(12.5, -23.43) * mm, "construction": true});
            skLineSegment(sketch, "E86", {"start": v(24.5, -23.43) * mm, "end": v(34.5, -23.43) * mm, "construction": true});
            skLineSegment(sketch, "E87", {"start": v(34.5, -23.43) * mm, "end": v(44.5, -23.43) * mm, "construction": true});
            skSolve(sketch);
        }
        {
            var Q0;
            Q0 = qSketchRegion(id + "F32", true);
            extrude(context, id + "F33", {"entities" : qUnion([Q0]), "operationType" : NewBodyOperationType.ADD, "depth" : 10.2 * mm});
        }
        {
            var Q0;
            Q0=makeQuery(id+"F9.imprint","IMPRINT",FACE,{"disambiguationData":[TD([[makeQuery(id+"F9.imprint","IMPRINT",EDGE,{"derivedFrom":sQuery(id+"F9.wireOp",EDGE,"E2")}),1.0]])]});
            var sketch = newSketch(context, id + "F34", { "sketchPlane" : qUnion([Q0])});
            skLineSegment(sketch, "E88.0", {"start": v(57.15, 56.9) * mm, "end": v(57.15, -56.91) * mm, "construction": true});
            skLineSegment(sketch, "E89.bottom", {"start": v(57.15, -39) * mm, "end": v(79.9, -39) * mm});
            skLineSegment(sketch, "E89.top", {"start": v(57.15, 39) * mm, "end": v(79.9, 39) * mm});
            skLineSegment(sketch, "E89.left", {"start": v(57.15, -39) * mm, "end": v(57.15, 39) * mm});
            skLineSegment(sketch, "E89.right", {"start": v(79.9, -39) * mm, "end": v(79.9, 39) * mm});
            skPoint(sketch, "E90", {"position": v(57.15, 0) * mm});
            skArc(sketch, "E91.0", {"start": v(44.46, -77) * mm, "mid": v(69.83, -55.05) * mm, "end": v(85.25, -25.25) * mm, "construction": true});
            skArc(sketch, "E92.0", {"start": v(88.92, 0) * mm, "mid": v(82.59, 32.95) * mm, "end": v(64.5, 61.2) * mm, "construction": true});
            skLineSegment(sketch, "E93.MirrorCS", {"start": v(-79.9, -39) * mm, "end": v(-79.9, 39) * mm});
            skLineSegment(sketch, "E94.MirrorCS", {"start": v(-57.15, 39) * mm, "end": v(-79.9, 39) * mm});
            skLineSegment(sketch, "E95.MirrorCS", {"start": v(-57.15, 56.9) * mm, "end": v(-57.15, -56.91) * mm, "construction": true});
            skLineSegment(sketch, "E96.MirrorCS", {"start": v(-57.15, -39) * mm, "end": v(-79.9, -39) * mm});
            skLineSegment(sketch, "E97.MirrorCS", {"start": v(-57.15, -39) * mm, "end": v(-57.15, 39) * mm});
            skSolve(sketch);
        }
        {
            var Q0;
            Q0 = qSketchRegion(id + "F34", true);
            var Q1;
            {var subQ4=sQuery(id+"F9.wireOp",EDGE,"E2");Q1=makeQuery(id+"F25.boolean.opBoolean","SPLIT",FACE,{"disambiguationData":[TD([makeQuery(id+"F10.opExtrude","SWEPT_FACE",FACE,{"disambiguationData":[OSD([subQ4])]})])],"derivedFrom":makeQuery(id+"F10.opExtrude","CAP_FACE",FACE,{"disambiguationData":[OSD([subQ4])],"isStart":false})});}
            extrude(context, id + "F35", {"entities" : qUnion([Q0]), "operationType" : NewBodyOperationType.REMOVE, "endBound" : BoundingType.UP_TO_SURFACE, "endBoundEntityFace" : qUnion([Q1]), "depth" : 25 * mm, "hasDraft" : true, "draftAngle" : 3 * degree, "draftPullDirection" : true});
        }
        {
            var Q0;
            {var subQ4=sQuery(id+"F9.wireOp",EDGE,"E2");Q0=makeQuery(id+"F25.boolean.opBoolean","SPLIT",FACE,{"disambiguationData":[TD([makeQuery(id+"F10.opExtrude","SWEPT_FACE",FACE,{"disambiguationData":[OSD([subQ4])]})])],"derivedFrom":makeQuery(id+"F10.opExtrude","CAP_FACE",FACE,{"disambiguationData":[OSD([subQ4])],"isStart":false})});}
            var sketch = newSketch(context, id + "F36", { "sketchPlane" : qUnion([Q0])});
            skLineSegment(sketch, "E98.0", {"start": v(-57.55, -38.6) * mm, "end": v(-79.5, -38.6) * mm, "construction": true});
            skLineSegment(sketch, "E99.0", {"start": v(-57.55, -38.6) * mm, "end": v(-57.55, 38.6) * mm, "construction": true});
            skLineSegment(sketch, "E100.0", {"start": v(-79.5, -38.6) * mm, "end": v(-79.5, 38.6) * mm, "construction": true});
            skLineSegment(sketch, "E101.0", {"start": v(-57.55, 38.6) * mm, "end": v(-79.5, 38.6) * mm, "construction": true});
            skLineSegment(sketch, "E102.0", {"start": v(-58.05, -38.1) * mm, "end": v(-58.05, 38.1) * mm});
            skLineSegment(sketch, "E102.1", {"start": v(-58.05, -38.1) * mm, "end": v(-79, -38.1) * mm});
            skLineSegment(sketch, "E102.2", {"start": v(-79, -38.1) * mm, "end": v(-79, 38.1) * mm});
            skLineSegment(sketch, "E102.3", {"start": v(-58.05, 38.1) * mm, "end": v(-79, 38.1) * mm});
            skLineSegment(sketch, "E103.MirrorCS", {"start": v(58.05, -38.1) * mm, "end": v(58.05, 38.1) * mm});
            skLineSegment(sketch, "E104.MirrorCS", {"start": v(58.05, -38.1) * mm, "end": v(79, -38.1) * mm});
            skLineSegment(sketch, "E105.MirrorCS", {"start": v(79, -38.1) * mm, "end": v(79, 38.1) * mm});
            skLineSegment(sketch, "E106.MirrorCS", {"start": v(58.05, 38.1) * mm, "end": v(79, 38.1) * mm});
            skSolve(sketch);
        }
        {
            var Q0;
            Q0 = qSketchRegion(id + "F36", true);
            extrude(context, id + "F37", {"entities" : qUnion([Q0]), "depth" : 14 * mm, "hasSecondDirection" : true, "secondDirectionOppositeDirection" : true, "secondDirectionDepth" : (2 * getVariable(context, 't')) * mm});
        }
        {
            var Q0;
            Q0=makeQuery(id+"F37.opExtrude","CAP_FACE",FACE,{"disambiguationData":[OSD([sQuery(id+"F36.wireOp",EDGE,"E102.0"),sQuery(id+"F36.wireOp",EDGE,"E102.1"),sQuery(id+"F36.wireOp",EDGE,"E102.2"),sQuery(id+"F36.wireOp",EDGE,"E102.3")])],"isStart":false});
            var Q1;
            Q1=makeQuery(id+"F37.opExtrude","CAP_FACE",FACE,{"disambiguationData":[OSD([sQuery(id+"F36.wireOp",EDGE,"E103.MirrorCS"),sQuery(id+"F36.wireOp",EDGE,"E104.MirrorCS"),sQuery(id+"F36.wireOp",EDGE,"E105.MirrorCS"),sQuery(id+"F36.wireOp",EDGE,"E106.MirrorCS")])],"isStart":false});
            shell(context, id + "F38", {"entities" : qUnion([Q0, Q1]), "thickness" : 1 * mm});
        }
        {
            var Q0;
            Q0=makeQuery(id+"F38.opShell","OFFSET_FACE",FACE,{"disambiguationData":[OSD([sQuery(id+"F36.wireOp",EDGE,"E102.0"),sQuery(id+"F36.wireOp",EDGE,"E102.1"),sQuery(id+"F36.wireOp",EDGE,"E102.2"),sQuery(id+"F36.wireOp",EDGE,"E102.3")])]});
            var sketch = newSketch(context, id + "F39", { "sketchPlane" : qUnion([Q0])});
            skLineSegment(sketch, "E107", {"start": v(-68.53, -37.1) * mm, "end": v(-68.53, 37.1) * mm, "construction": true});
            skLineSegment(sketch, "E108", {"start": v(-59.05, 0) * mm, "end": v(-78, 0) * mm, "construction": true});
            skCircle(sketch, "E109", {"center": v(-68.53, 0) * mm, "radius": 1.6 * mm});
            skCircle(sketch, "E110.MirrorC", {"center": v(68.53, 0) * mm, "radius": 1.6 * mm});
            skLineSegment(sketch, "E111", {"start": v(0, 0) * mm, "end": v(68.53, 0) * mm, "construction": true});
            skSolve(sketch);
        }
        {
            var Q0;
            Q0 = qSketchRegion(id + "F39", true);
            var Q1;
            Q1=makeQuery(id+"F37.opExtrude","CAP_FACE",FACE,{"disambiguationData":[OSD([sQuery(id+"F36.wireOp",EDGE,"E103.MirrorCS"),sQuery(id+"F36.wireOp",EDGE,"E104.MirrorCS"),sQuery(id+"F36.wireOp",EDGE,"E105.MirrorCS"),sQuery(id+"F36.wireOp",EDGE,"E106.MirrorCS")])],"isStart":true});
            extrude(context, id + "F40", {"entities" : qUnion([Q0]), "operationType" : NewBodyOperationType.REMOVE, "endBound" : BoundingType.UP_TO_SURFACE, "oppositeDirection" : true, "endBoundEntityFace" : qUnion([Q1]), "depth" : 25 * mm});
        }
        {
            var Q0;
            Q0=makeQuery(id+"F38.opShell","OFFSET_FACE",FACE,{"disambiguationData":[OSD([sQuery(id+"F36.wireOp",EDGE,"E102.1")])]});
            var sketch = newSketch(context, id + "F41", { "sketchPlane" : qUnion([Q0])});
            skLineSegment(sketch, "E112", {"start": v(68.53, 232.57) * mm, "end": v(68.53, 214.49) * mm, "construction": true});
            skLineSegment(sketch, "E113", {"start": v(59.05, 223.53) * mm, "end": v(78, 223.53) * mm, "construction": true});
            skCircle(sketch, "E114", {"center": v(68.53, 223.53) * mm, "radius": 9 * mm});
            skCircle(sketch, "E115.MirrorC", {"center": v(-68.53, 223.53) * mm, "radius": 9 * mm});
            skSolve(sketch);
        }
        {
            var Q0;
            Q0 = qSketchRegion(id + "F41", true);
            extrude(context, id + "F42", {"entities" : qUnion([Q0]), "depth" : 70 * mm, "hasSecondDirection" : true, "secondDirectionOppositeDirection" : false, "secondDirectionDepth" : 5 * mm});
        }
        {
            var Q0;
            Q0=makeQuery(id+"F9.imprint","IMPRINT",FACE,{"disambiguationData":[TD([[makeQuery(id+"F9.imprint","IMPRINT",EDGE,{"derivedFrom":sQuery(id+"F9.wireOp",EDGE,"E2")}),1.0]])]});
            var sketch = newSketch(context, id + "F43", { "sketchPlane" : qUnion([Q0])});
            skArc(sketch, "E116.0", {"start": v(44.46, -77) * mm, "mid": v(45.96, -76.12) * mm, "end": v(47.45, -75.2) * mm, "construction": true});
            skArc(sketch, "E117.0", {"start": v(-79.9, -39) * mm, "mid": v(-79.13, -40.55) * mm, "end": v(-78.33, -42.09) * mm, "construction": true});
            skArc(sketch, "E118.0", {"start": v(-88.92, 0) * mm, "mid": v(-88.9, -1.75) * mm, "end": v(-88.85, -3.5) * mm, "construction": true});
            skArc(sketch, "E119.0", {"start": v(79.9, -39) * mm, "mid": v(82.22, -33.86) * mm, "end": v(84.2, -28.58) * mm});
            skLineSegment(sketch, "E120", {"start": v(0, 0) * mm, "end": v(44.46, -77) * mm, "construction": true});
            skLineSegment(sketch, "E121", {"start": v(0, 0) * mm, "end": v(85.25, -25.25) * mm, "construction": true});
            skLineSegment(sketch, "E122", {"start": v(0, 0) * mm, "end": v(47.45, -75.2) * mm, "construction": true});
            skLineSegment(sketch, "E123", {"start": v(0, 0) * mm, "end": v(84.2, -28.58) * mm, "construction": true});
            skLineSegment(sketch, "E124", {"start": v(0, 0) * mm, "end": v(64.95, -64.39) * mm, "construction": true});
            skLineSegment(sketch, "E125", {"start": v(0, 0) * mm, "end": v(77.77, -48.13) * mm, "construction": true});
            skLineSegment(sketch, "E126", {"start": v(47.45, -75.2) * mm, "end": v(48.27, -76.5) * mm});
            skLineSegment(sketch, "E127", {"start": v(63.15, -62.6) * mm, "end": v(64.24, -63.69) * mm});
            skLineSegment(sketch, "E128", {"start": v(75.61, -46.79) * mm, "end": v(76.92, -47.6) * mm});
            skLineSegment(sketch, "E129", {"start": v(84.2, -28.58) * mm, "end": v(85.66, -29.08) * mm});
            skLineSegment(sketch, "E130", {"start": v(0, 0) * mm, "end": v(-64.5, -61.2) * mm, "construction": true});
            skLineSegment(sketch, "E131", {"start": v(0, 0) * mm, "end": v(-88.92, 0) * mm, "construction": true});
            skLineSegment(sketch, "E132", {"start": v(0, 0) * mm, "end": v(-80.57, -43.29) * mm, "construction": true});
            skLineSegment(sketch, "E133", {"start": v(0, 0) * mm, "end": v(-88.24, -24.06) * mm, "construction": true});
            skLineSegment(sketch, "E134", {"start": v(0, 0) * mm, "end": v(-68.76, -60.3) * mm, "construction": true});
            skLineSegment(sketch, "E135", {"start": v(0, 0) * mm, "end": v(-91.39, -3.6) * mm, "construction": true});
            skLineSegment(sketch, "E136", {"start": v(-68.76, -60.3) * mm, "end": v(-68.01, -59.64) * mm, "construction": true});
            skLineSegment(sketch, "E137", {"start": v(-80.57, -43.29) * mm, "end": v(-79.69, -42.82) * mm, "construction": true});
            skLineSegment(sketch, "E138", {"start": v(-88.24, -24.06) * mm, "end": v(-87.27, -23.8) * mm, "construction": true});
            skLineSegment(sketch, "E139", {"start": v(-91.39, -3.6) * mm, "end": v(-90.4, -3.55) * mm, "construction": true});
            skArc(sketch, "E140", {"start": v(-68.76, -60.3) * mm, "mid": v(-13.12, -90.51) * mm, "end": v(48.8, -77.35) * mm, "construction": true});
            skArc(sketch, "E141", {"start": v(-80.57, -43.29) * mm, "mid": v(-75.15, -52.13) * mm, "end": v(-68.76, -60.3) * mm, "construction": true});
            skArc(sketch, "E142", {"start": v(-88.24, -24.06) * mm, "mid": v(-84.95, -33.9) * mm, "end": v(-80.57, -43.29) * mm, "construction": true});
            skArc(sketch, "E143", {"start": v(-91.39, -3.6) * mm, "mid": v(-90.4, -13.91) * mm, "end": v(-88.24, -24.06) * mm, "construction": true});
            skArc(sketch, "E144", {"start": v(48.8, -77.35) * mm, "mid": v(57.25, -71.33) * mm, "end": v(64.95, -64.39) * mm, "construction": true});
            skArc(sketch, "E145", {"start": v(64.95, -64.39) * mm, "mid": v(71.83, -56.62) * mm, "end": v(77.77, -48.13) * mm, "construction": true});
            skArc(sketch, "E146", {"start": v(77.77, -48.13) * mm, "mid": v(82.72, -39.01) * mm, "end": v(86.6, -29.4) * mm, "construction": true});
            skArc(sketch, "E147", {"start": v(86.6, -29.4) * mm, "mid": v(13.12, 90.51) * mm, "end": v(-91.39, -3.6) * mm, "construction": true});
            skArc(sketch, "E148", {"start": v(-85.79, -23.39) * mm, "mid": v(-83.21, -31.33) * mm, "end": v(-79.9, -39) * mm, "construction": true});
            skArc(sketch, "E149", {"start": v(-66.85, -58.63) * mm, "mid": v(-65.69, -59.93) * mm, "end": v(-64.5, -61.2) * mm, "construction": true});
            skArc(sketch, "E150", {"start": v(-78.33, -42.09) * mm, "mid": v(-73.06, -50.68) * mm, "end": v(-66.85, -58.63) * mm});
            skArc(sketch, "E151", {"start": v(-88.85, -3.5) * mm, "mid": v(-87.88, -13.53) * mm, "end": v(-85.79, -23.39) * mm});
            skArc(sketch, "E152", {"start": v(47.45, -75.2) * mm, "mid": v(55.65, -69.34) * mm, "end": v(63.15, -62.6) * mm});
            skArc(sketch, "E153", {"start": v(63.15, -62.6) * mm, "mid": v(69.83, -55.05) * mm, "end": v(75.61, -46.79) * mm, "construction": true});
            skArc(sketch, "E154", {"start": v(75.61, -46.79) * mm, "mid": v(77.86, -42.95) * mm, "end": v(79.9, -39) * mm});
            skArc(sketch, "E155", {"start": v(84.2, -28.58) * mm, "mid": v(84.74, -26.92) * mm, "end": v(85.25, -25.25) * mm, "construction": true});
            skArc(sketch, "E156.0", {"start": v(48.27, -76.5) * mm, "mid": v(56.62, -70.55) * mm, "end": v(64.24, -63.69) * mm});
            skArc(sketch, "E157.0", {"start": v(76.92, -47.6) * mm, "mid": v(81.82, -38.59) * mm, "end": v(85.66, -29.08) * mm});
            skArc(sketch, "E158.0", {"start": v(-79.69, -42.82) * mm, "mid": v(-74.33, -51.56) * mm, "end": v(-68.01, -59.64) * mm});
            skArc(sketch, "E159.0", {"start": v(-90.4, -3.55) * mm, "mid": v(-89.4, -13.76) * mm, "end": v(-87.27, -23.8) * mm});
            skLineSegment(sketch, "E160", {"start": v(76.92, -47.6) * mm, "end": v(77.77, -48.13) * mm, "construction": true});
            skLineSegment(sketch, "E161", {"start": v(85.66, -29.08) * mm, "end": v(86.6, -29.4) * mm, "construction": true});
            skLineSegment(sketch, "E162", {"start": v(64.24, -63.69) * mm, "end": v(64.95, -64.39) * mm, "construction": true});
            skLineSegment(sketch, "E163", {"start": v(48.27, -76.5) * mm, "end": v(48.8, -77.35) * mm, "construction": true});
            skLineSegment(sketch, "E164", {"start": v(-68.01, -59.64) * mm, "end": v(-66.85, -58.63) * mm});
            skLineSegment(sketch, "E165", {"start": v(-79.69, -42.82) * mm, "end": v(-78.33, -42.09) * mm});
            skLineSegment(sketch, "E166", {"start": v(-87.27, -23.8) * mm, "end": v(-85.79, -23.39) * mm});
            skLineSegment(sketch, "E167", {"start": v(-90.4, -3.55) * mm, "end": v(-88.85, -3.5) * mm});
            skSolve(sketch);
        }
        {
            var Q0;
            Q0 = qSketchRegion(id + "F43", true);
            extrude(context, id + "F44", {"entities" : qUnion([Q0]), "operationType" : NewBodyOperationType.ADD, "oppositeDirection" : true, "depth" : 2 * mm, "hasDraft" : true, "draftAngle" : 3 * degree, "draftPullDirection" : true});
        }
    });
